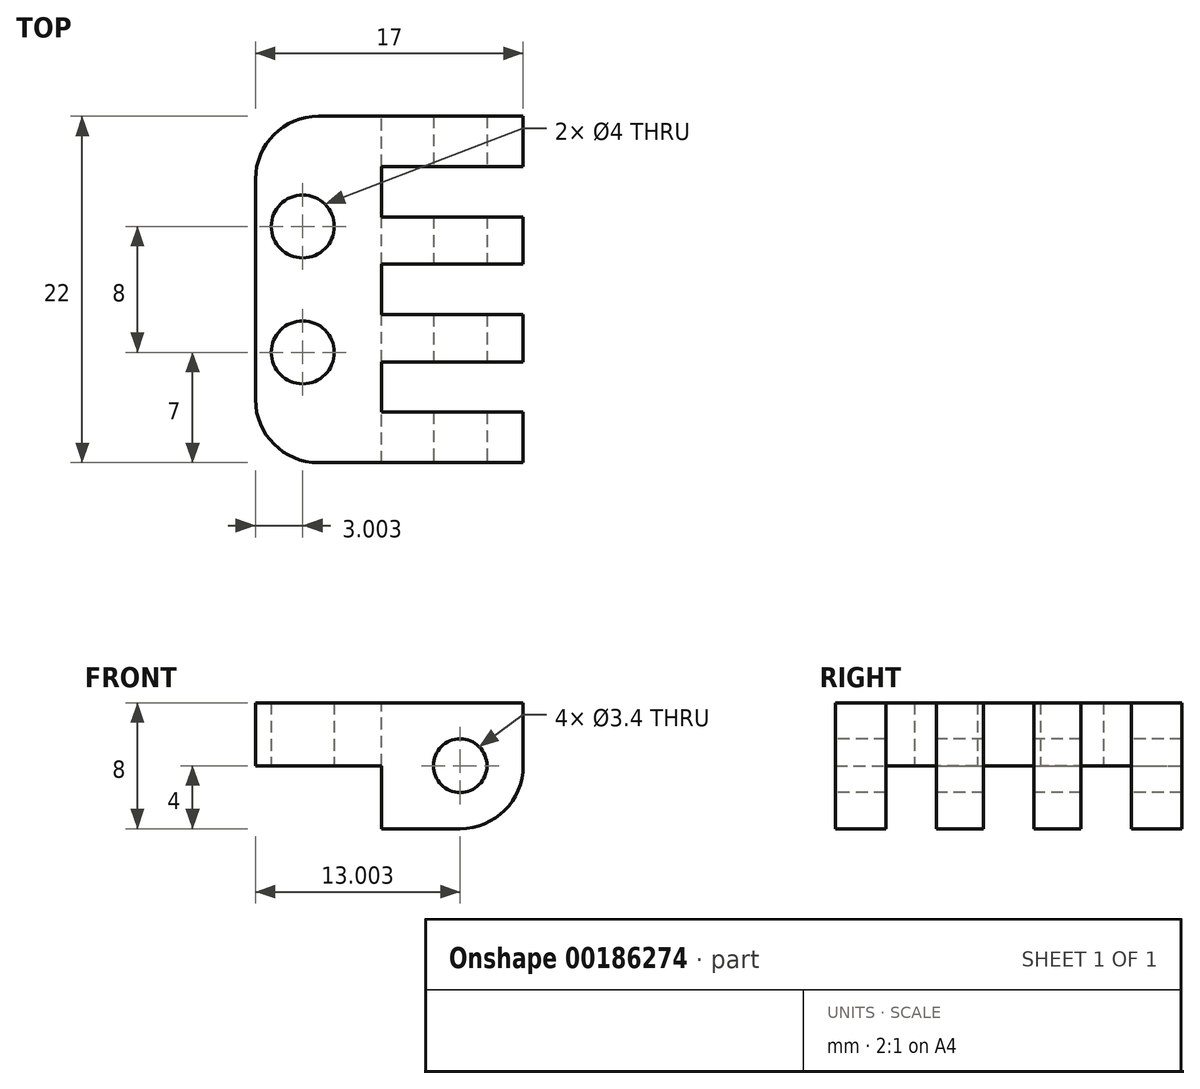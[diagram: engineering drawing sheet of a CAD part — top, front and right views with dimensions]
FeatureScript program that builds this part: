
annotation { "Feature Type Name" : "Feature", "Feature Type Description" : "" }
export const myFeature = defineFeature(function(context is Context, id is Id, definition is map)
    precondition{}
    {
        {
            var Q0;
            Q0=qCreatedBy(makeId("Top.planeOp"),FACE);
            var sketch = newSketch(context, id + "F0", { "sketchPlane" : qUnion([Q0])});
            skLineSegment(sketch, "E0.bottom", {"start": v(-5.17, -9) * mm, "end": v(1.83, -9) * mm});
            skLineSegment(sketch, "E0.top", {"start": v(-5.17, 9) * mm, "end": v(1.83, 9) * mm});
            skLineSegment(sketch, "E0.left", {"start": v(-5.17, -9) * mm, "end": v(-5.17, 9) * mm});
            skLineSegment(sketch, "E0.right", {"start": v(1.83, -9) * mm, "end": v(1.83, 9) * mm});
            skPoint(sketch, "E1", {"position": v(-2.17, 4) * mm});
            skPoint(sketch, "E2", {"position": v(-2.17, -4) * mm});
            skLineSegment(sketch, "E3.bottom", {"start": v(1.83, 9) * mm, "end": v(11.83, 9) * mm});
            skLineSegment(sketch, "E3.top", {"start": v(1.83, -9) * mm, "end": v(11.83, -9) * mm});
            skLineSegment(sketch, "E3.left", {"start": v(1.83, 9) * mm, "end": v(1.83, -9) * mm});
            skLineSegment(sketch, "E3.right", {"start": v(11.83, 9) * mm, "end": v(11.83, -9) * mm});
            skCircle(sketch, "E4", {"center": v(-2.17, 4) * mm, "radius": 2 * mm});
            skCircle(sketch, "E5", {"center": v(-2.17, -4) * mm, "radius": 2 * mm});
            skSolve(sketch);
        }
        {
            var Q0;
            Q0=makeQuery(id+"F0.imprint","IMPRINT",FACE,{"disambiguationData":[TD([[makeQuery(id+"F0.imprint","IMPRINT",EDGE,{"derivedFrom":sQuery(id+"F0.wireOp",EDGE,"E0.bottom")}),1.0]])]});
            var Q1;
            Q1=makeQuery(id+"F0.imprint","IMPRINT",FACE,{"disambiguationData":[TD([[makeQuery(id+"F0.imprint","IMPRINT",EDGE,{"derivedFrom":sQuery(id+"F0.wireOp",EDGE,"E3.bottom")}),-1.0]])]});
            extrude(context, id + "F1", {"entities" : qUnion([Q0, Q1]), "depth" : 8 * mm, "offsetDistance" : 25 * mm});
        }
        {
            var Q0;
            Q0=makeQuery(id+"F1.opExtrude","SWEPT_FACE",FACE,{"disambiguationData":[OSD([sQuery(id+"F0.wireOp",EDGE,"E0.bottom"),sQuery(id+"F0.wireOp",EDGE,"E3.top")])]});
            var sketch = newSketch(context, id + "F2", { "sketchPlane" : qUnion([Q0])});
            skPoint(sketch, "E6", {"position": v(11.83, 4) * mm});
            skPoint(sketch, "E7", {"position": v(7.83, 4) * mm});
            skCircle(sketch, "E8", {"center": v(7.83, 4) * mm, "radius": 1.6 * mm});
            skSolve(sketch);
        }
        {
            var Q0;
            Q0=sQuery(id+"F2.wireOp",VERTEX,"E7");
            var Q1;
            Q1=makeQuery(id+"F1.opExtrude","SWEPT_BODY",BODY,{"disambiguationData":[OSD([sQuery(id+"F0.wireOp",EDGE,"E0.bottom"),sQuery(id+"F0.wireOp",EDGE,"E0.top"),sQuery(id+"F0.wireOp",EDGE,"E0.left"),sQuery(id+"F0.wireOp",EDGE,"E3.bottom"),sQuery(id+"F0.wireOp",EDGE,"E3.top"),sQuery(id+"F0.wireOp",EDGE,"E3.right"),sQuery(id+"F0.wireOp",EDGE,"E4"),sQuery(id+"F0.wireOp",EDGE,"E5")])]});
            hole(context, id + "F3", {"style" : HoleStyle.SIMPLE, "endStyle" : HoleEndStyle.THROUGH, "standardTappedOrClearance" : lookupTablePath({ "fit" : "Normal", "standard" : "ISO", "size" : "M3", "type" : "Clearance" }), "standardBlindInLast" : lookupTablePath({ "fit" : "Normal", "standard" : "ISO", "engagement" : "75%", "pitch" : "0.5 mm", "size" : "M3", "type" : "Clearance & tapped" }), "holeDiameter" : 3.4 * mm, "majorDiameter" : 5 * mm, "isTappedThrough" : true, "tappedDepth" : 12 * mm, "tapClearance" : 3, "startFromSketch" : true, "locations" : qUnion([Q0]), "scope" : qUnion([Q1])});
        }
        {
            var Q0;
            Q0=makeQuery(id+"F1.opExtrude","CAP_FACE",FACE,{"disambiguationData":[OSD([sQuery(id+"F0.wireOp",EDGE,"E0.bottom"),sQuery(id+"F0.wireOp",EDGE,"E0.top"),sQuery(id+"F0.wireOp",EDGE,"E0.left"),sQuery(id+"F0.wireOp",EDGE,"E3.bottom"),sQuery(id+"F0.wireOp",EDGE,"E3.top"),sQuery(id+"F0.wireOp",EDGE,"E3.right"),sQuery(id+"F0.wireOp",EDGE,"E4"),sQuery(id+"F0.wireOp",EDGE,"E5")])],"isStart":false});
            var sketch = newSketch(context, id + "F4", { "sketchPlane" : qUnion([Q0])});
            skPoint(sketch, "E9", {"position": v(11.83, 0) * mm});
            skPoint(sketch, "E10", {"position": v(11.83, -1.6) * mm});
            skPoint(sketch, "E11", {"position": v(11.83, 1.6) * mm});
            skPoint(sketch, "E12", {"position": v(11.83, -4.6) * mm});
            skPoint(sketch, "E13", {"position": v(11.83, 4.6) * mm});
            skPoint(sketch, "E14", {"position": v(11.83, 7.8) * mm});
            skPoint(sketch, "E15", {"position": v(11.83, -7.8) * mm});
            skPoint(sketch, "E16", {"position": v(2.83, 1.6) * mm});
            skPoint(sketch, "E17", {"position": v(2.83, -1.6) * mm});
            skLineSegment(sketch, "E18", {"start": v(11.83, 1.6) * mm, "end": v(2.83, 1.6) * mm});
            skLineSegment(sketch, "E19", {"start": v(2.83, -1.6) * mm, "end": v(2.83, 1.6) * mm});
            skLineSegment(sketch, "E20", {"start": v(2.83, -1.6) * mm, "end": v(11.83, -1.6) * mm});
            skPoint(sketch, "E21", {"position": v(2.83, -4.6) * mm});
            skPoint(sketch, "E22", {"position": v(2.83, -7.8) * mm});
            skPoint(sketch, "E23", {"position": v(2.83, 4.6) * mm});
            skPoint(sketch, "E24", {"position": v(2.83, 7.8) * mm});
            skLineSegment(sketch, "E25", {"start": v(11.83, 4.6) * mm, "end": v(2.83, 4.6) * mm});
            skLineSegment(sketch, "E26", {"start": v(2.83, 7.8) * mm, "end": v(2.83, 4.6) * mm});
            skLineSegment(sketch, "E27", {"start": v(2.83, 7.8) * mm, "end": v(11.83, 7.8) * mm});
            skLineSegment(sketch, "E28", {"start": v(2.83, -4.6) * mm, "end": v(11.83, -4.6) * mm});
            skLineSegment(sketch, "E29", {"start": v(2.83, -4.6) * mm, "end": v(2.83, -7.8) * mm});
            skLineSegment(sketch, "E30", {"start": v(2.83, -7.8) * mm, "end": v(11.83, -7.8) * mm});
            skSolve(sketch);
        }
        {
            var Q0;
            {var subQ0=sQuery(id+"F4.wireOp",EDGE,"E25");Q0=makeQuery(id+"F4.imprint","IMPRINT",FACE,{"disambiguationData":[TD([[makeQuery(id+"F4.imprint","IMPRINT",EDGE,{"derivedFrom":subQ0}),-1.0]])]});}
            var Q1;
            {var subQ0=sQuery(id+"F4.wireOp",EDGE,"E18");Q1=makeQuery(id+"F4.imprint","IMPRINT",FACE,{"disambiguationData":[TD([[makeQuery(id+"F4.imprint","IMPRINT",EDGE,{"derivedFrom":subQ0}),1.0]])]});}
            var Q2;
            {var subQ0=sQuery(id+"F4.wireOp",EDGE,"E28");Q2=makeQuery(id+"F4.imprint","IMPRINT",FACE,{"disambiguationData":[TD([[makeQuery(id+"F4.imprint","IMPRINT",EDGE,{"derivedFrom":subQ0}),-1.0]])]});}
            extrude(context, id + "F5", {"entities" : qUnion([Q0, Q1, Q2]), "operationType" : NewBodyOperationType.REMOVE, "oppositeDirection" : true, "depth" : 25 * mm, "offsetDistance" : 25 * mm});
        }
        {
            var Q0;
            Q0=makeQuery(id+"F1.opExtrude","SWEPT_FACE",FACE,{"disambiguationData":[OSD([sQuery(id+"F0.wireOp",EDGE,"E0.bottom"),sQuery(id+"F0.wireOp",EDGE,"E3.top")])]});
            extrude(context, id + "F6", {"entities" : qUnion([Q0]), "operationType" : NewBodyOperationType.ADD, "depth" : 2 * mm, "offsetDistance" : 25 * mm});
        }
        {
            var Q0;
            Q0=makeQuery(id+"F1.opExtrude","SWEPT_FACE",FACE,{"disambiguationData":[OSD([sQuery(id+"F0.wireOp",EDGE,"E0.top"),sQuery(id+"F0.wireOp",EDGE,"E3.bottom")])]});
            extrude(context, id + "F7", {"entities" : qUnion([Q0]), "operationType" : NewBodyOperationType.ADD, "depth" : 2 * mm, "offsetDistance" : 25 * mm});
        }
        {
            var Q0;
            {var subQ0=sQuery(id+"F0.wireOp",EDGE,"E3.bottom");var subQ1=sQuery(id+"F0.wireOp",EDGE,"E0.top");var subQ2=sQuery(id+"F0.wireOp",EDGE,"E3.top");var subQ3=sQuery(id+"F0.wireOp",EDGE,"E0.bottom");Q0=makeQuery(id+"F7.boolean.opBoolean","MERGE",FACE,{"derivedFrom":[makeQuery(id+"F6.boolean.opBoolean","MERGE",FACE,{"derivedFrom":[makeQuery(id+"F1.opExtrude","CAP_FACE",FACE,{"disambiguationData":[OSD([subQ3,subQ1,sQuery(id+"F0.wireOp",EDGE,"E0.left"),subQ0,subQ2,sQuery(id+"F0.wireOp",EDGE,"E3.right"),sQuery(id+"F0.wireOp",EDGE,"E4"),sQuery(id+"F0.wireOp",EDGE,"E5")])],"isStart":true}),makeQuery(id+"F6.opExtrude","SWEPT_FACE",FACE,{"disambiguationData":[OSD([subQ3,subQ2]),TDD([makeQuery(id+"F1.opExtrude","CAP_EDGE",EDGE,{"disambiguationData":[OSD([subQ3,subQ2])],"isStart":true})])]})]}),makeQuery(id+"F7.opExtrude","SWEPT_FACE",FACE,{"disambiguationData":[OSD([subQ1,subQ0]),TDD([makeQuery(id+"F1.opExtrude","CAP_EDGE",EDGE,{"disambiguationData":[OSD([subQ1,subQ0])],"isStart":true})])]})]});}
            var sketch = newSketch(context, id + "F8", { "sketchPlane" : qUnion([Q0])});
            skPoint(sketch, "E31", {"position": v(2.83, 11) * mm});
            skPoint(sketch, "E32", {"position": v(2.83, -11) * mm});
            skLineSegment(sketch, "E33", {"start": v(2.83, 11) * mm, "end": v(2.83, -11) * mm});
            skSolve(sketch);
        }
        {
            var Q0;
            {var subQ4=sQuery(id+"F8.wireOp",EDGE,"E33");Q0=makeQuery(id+"F8.imprint","IMPRINT",FACE,{"disambiguationData":[TD([[makeQuery(id+"F8.imprint","IMPRINT",EDGE,{"derivedFrom":subQ4}),-1.0]])]});}
            extrude(context, id + "F9", {"entities" : qUnion([Q0]), "operationType" : NewBodyOperationType.REMOVE, "oppositeDirection" : true, "depth" : 4 * mm, "offsetDistance" : 25 * mm});
        }
        {
            var Q0;
            Q0=makeQuery(id+"F6.opExtrude","CAP_EDGE",EDGE,{"disambiguationData":[OSD([sQuery(id+"F0.wireOp",EDGE,"E0.bottom"),sQuery(id+"F0.wireOp",EDGE,"E0.left")])],"isStart":false});
            var Q1;
            Q1=makeQuery(id+"F7.opExtrude","CAP_EDGE",EDGE,{"disambiguationData":[OSD([sQuery(id+"F0.wireOp",EDGE,"E0.top"),sQuery(id+"F0.wireOp",EDGE,"E0.left")])],"isStart":false});
            var Q2;
            {var subQ2=sQuery(id+"F8.wireOp",EDGE,"E33");Q2=makeQuery(id+"F9.boolean.opBoolean","COPY",EDGE,{"disambiguationData":[TD([makeQuery(id+"F5.boolean.opBoolean","COPY",FACE,{"derivedFrom":makeQuery(id+"F5.opExtrude","SWEPT_FACE",FACE,{"disambiguationData":[OSD([sQuery(id+"F4.wireOp",EDGE,"E30")])]})})])],"derivedFrom":makeQuery(id+"F9.opExtrude","CAP_EDGE",EDGE,{"disambiguationData":[OSD([subQ2])],"isStart":true})});}
            var Q3;
            {var subQ2=sQuery(id+"F8.wireOp",EDGE,"E33");Q3=makeQuery(id+"F9.boolean.opBoolean","COPY",EDGE,{"disambiguationData":[TD([makeQuery(id+"F5.boolean.opBoolean","COPY",FACE,{"derivedFrom":makeQuery(id+"F5.opExtrude","SWEPT_FACE",FACE,{"disambiguationData":[OSD([sQuery(id+"F4.wireOp",EDGE,"E20")])]})})])],"derivedFrom":makeQuery(id+"F9.opExtrude","CAP_EDGE",EDGE,{"disambiguationData":[OSD([subQ2])],"isStart":true})});}
            var Q4;
            {var subQ2=sQuery(id+"F8.wireOp",EDGE,"E33");Q4=makeQuery(id+"F9.boolean.opBoolean","COPY",EDGE,{"disambiguationData":[TD([makeQuery(id+"F5.boolean.opBoolean","COPY",FACE,{"derivedFrom":makeQuery(id+"F5.opExtrude","SWEPT_FACE",FACE,{"disambiguationData":[OSD([sQuery(id+"F4.wireOp",EDGE,"E18")])]})})])],"derivedFrom":makeQuery(id+"F9.opExtrude","CAP_EDGE",EDGE,{"disambiguationData":[OSD([subQ2])],"isStart":true})});}
            var Q5;
            {var subQ2=sQuery(id+"F8.wireOp",EDGE,"E33");Q5=makeQuery(id+"F9.boolean.opBoolean","COPY",EDGE,{"disambiguationData":[TD([makeQuery(id+"F5.boolean.opBoolean","COPY",FACE,{"derivedFrom":makeQuery(id+"F5.opExtrude","SWEPT_FACE",FACE,{"disambiguationData":[OSD([sQuery(id+"F4.wireOp",EDGE,"E27")])]})})])],"derivedFrom":makeQuery(id+"F9.opExtrude","CAP_EDGE",EDGE,{"disambiguationData":[OSD([subQ2])],"isStart":true})});}
            var Q6;
            {var subQ0=sQuery(id+"F0.wireOp",EDGE,"E3.right");var subQ1=sQuery(id+"F0.wireOp",EDGE,"E3.top");Q6=makeQuery(id+"F6.boolean.opBoolean","MERGE",EDGE,{"derivedFrom":[makeQuery(id+"F5.boolean.opBoolean","SPLIT",EDGE,{"disambiguationData":[TD([makeQuery(id+"F5.opExtrude","SWEPT_FACE",FACE,{"disambiguationData":[OSD([sQuery(id+"F4.wireOp",EDGE,"E30")])]})])],"derivedFrom":makeQuery(id+"F1.opExtrude","CAP_EDGE",EDGE,{"disambiguationData":[OSD([subQ0])],"isStart":true})}),makeQuery(id+"F6.opExtrude","SWEPT_EDGE",EDGE,{"disambiguationData":[OSD([subQ1,subQ0]),TDD([makeQuery(id+"F1.opExtrude","CAP_VERTEX",VERTEX,{"disambiguationData":[OSD([subQ1,subQ0])],"isStart":true})])]})]});}
            var Q7;
            {var subQ0=sQuery(id+"F0.wireOp",EDGE,"E3.right");Q7=makeQuery(id+"F5.boolean.opBoolean","SPLIT",EDGE,{"disambiguationData":[TD([makeQuery(id+"F5.opExtrude","SWEPT_FACE",FACE,{"disambiguationData":[OSD([sQuery(id+"F4.wireOp",EDGE,"E20")])]})])],"derivedFrom":makeQuery(id+"F1.opExtrude","CAP_EDGE",EDGE,{"disambiguationData":[OSD([subQ0])],"isStart":true})});}
            var Q8;
            {var subQ0=sQuery(id+"F0.wireOp",EDGE,"E3.right");Q8=makeQuery(id+"F5.boolean.opBoolean","SPLIT",EDGE,{"disambiguationData":[TD([makeQuery(id+"F5.opExtrude","SWEPT_FACE",FACE,{"disambiguationData":[OSD([sQuery(id+"F4.wireOp",EDGE,"E18")])]})])],"derivedFrom":makeQuery(id+"F1.opExtrude","CAP_EDGE",EDGE,{"disambiguationData":[OSD([subQ0])],"isStart":true})});}
            var Q9;
            {var subQ0=sQuery(id+"F0.wireOp",EDGE,"E3.right");var subQ1=sQuery(id+"F0.wireOp",EDGE,"E3.bottom");Q9=makeQuery(id+"F7.boolean.opBoolean","MERGE",EDGE,{"derivedFrom":[makeQuery(id+"F5.boolean.opBoolean","SPLIT",EDGE,{"disambiguationData":[TD([makeQuery(id+"F5.opExtrude","SWEPT_FACE",FACE,{"disambiguationData":[OSD([sQuery(id+"F4.wireOp",EDGE,"E27")])]})])],"derivedFrom":makeQuery(id+"F1.opExtrude","CAP_EDGE",EDGE,{"disambiguationData":[OSD([subQ0])],"isStart":true})}),makeQuery(id+"F7.opExtrude","SWEPT_EDGE",EDGE,{"disambiguationData":[OSD([subQ1,subQ0]),TDD([makeQuery(id+"F1.opExtrude","CAP_VERTEX",VERTEX,{"disambiguationData":[OSD([subQ1,subQ0])],"isStart":true})])]})]});}
            fillet(context, id + "F10", {"entities" : qUnion([Q0, Q1, Q2, Q3, Q4, Q5, Q6, Q7, Q8, Q9]), "tangentPropagation" : true, "radius" : 4 * mm, "defaultsChanged" : false, "vertexSettings" : [], "allowEdgeOverflow" : false});
        }
    });
